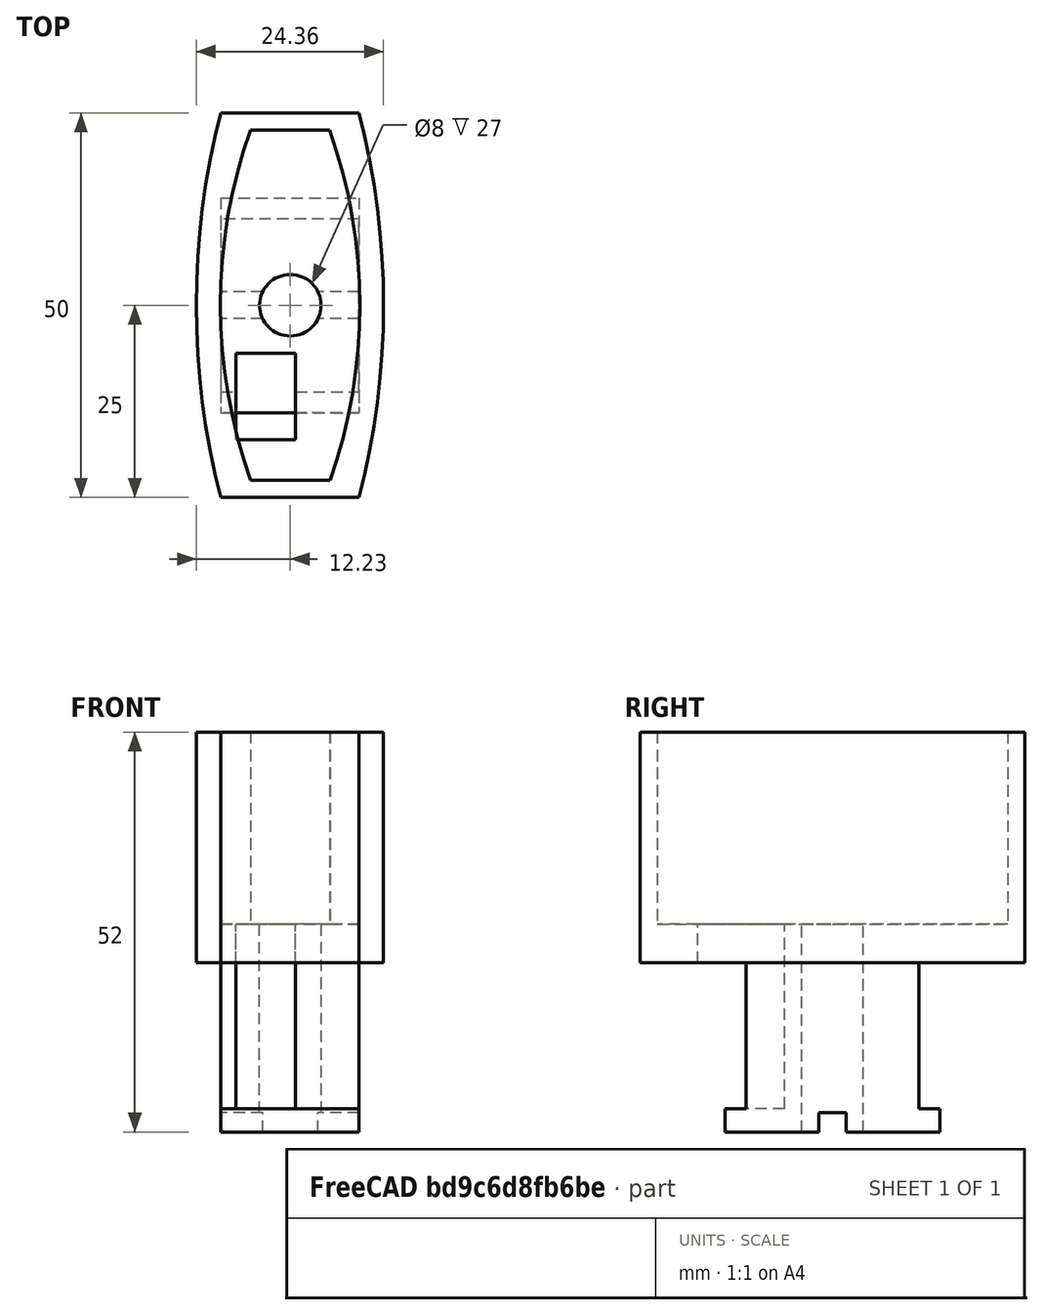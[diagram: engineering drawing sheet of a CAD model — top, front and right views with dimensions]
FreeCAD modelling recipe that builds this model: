
FCSTD DOCUMENT  (FreeCAD 0.18R4 (GitTag))
Label: theta_v_holder
License: All rights reserved
LicenseURL: http://en.wikipedia.org/wiki/All_rights_reserved
objects: Sketcher::SketchObject×7, PartDesign::Pocket×4, PartDesign::Pad×3, PartDesign::Body×1
note: 22 computed .brp shape members not serialized (recipe doc carries the construction recipe); baked Part::Feature solids carry a one-line shape summary decoded from their .brp

FEATURE [Sketcher::SketchObject] Sketch  label="base_sketch"
  MapMode = 5
  Support = -> [XY_Plane]
  sketch-geometry (4):
    g0: LineSegment StartX=0 StartY=0 StartZ=0 EndX=18 EndY=0 EndZ=0
    g1: LineSegment StartX=18 StartY=50 StartZ=0 EndX=0 EndY=50 EndZ=0
    g2: ArcOfCircle CenterX=-78.8246 CenterY=25 CenterZ=0 NormalX=0 NormalY=0 NormalZ=1 AngleXU=0 Radius=100 StartAngle=6.03051 EndAngle=6.53587
    g3: ArcOfCircle CenterX=96.8246 CenterY=25 CenterZ=0 NormalX=0 NormalY=0 NormalZ=1 AngleXU=0 Radius=100 StartAngle=2.88891 EndAngle=3.39427
  constraints (13):
    c: Horizontal(g0)
    c: Horizontal(g1)
    c: Coincident(g0,g-1)
    c: Distance(g1) = 18
    c: Equal(g0,g1)
    c: Coincident(g2,g0)
    c: Coincident(g2,g1)
    c: DistanceY(g0,g1) = 50
    c: Radius(g2) = 100
    c: Coincident(g3,g1)
    c: Coincident(g3,g0)
    c: Equal(g3,g2)
    c: DistanceX(g0,g1) = 0
FEATURE [PartDesign::Pad] Pad
  Length = 30
  Length2 = 100
  Profile = -> Sketch
  Reversed = true
  Type = 0
FEATURE [Sketcher::SketchObject] Sketch001
  MapMode = 5
  Support = -> [XY_Plane]
  sketch-geometry (5):
    g0: LineSegment StartX=3.9 StartY=2.225 StartZ=0 EndX=14.2 EndY=2.225 EndZ=0
    g1: LineSegment StartX=14.15 StartY=47.775 StartZ=0 EndX=3.85 EndY=47.775 EndZ=0
    g2: LineSegment StartX=-0.05 StartY=25 StartZ=0 EndX=18.1 EndY=25 EndZ=0
    g3: ArcOfCircle CenterX=67.9891 CenterY=25.0704 CenterZ=0 NormalX=0 NormalY=0 NormalZ=1 AngleXU=0 Radius=68.0391 StartAngle=2.80137 EndAngle=3.48401
    g4: ArcOfCircle CenterX=-49.9391 CenterY=24.9296 CenterZ=0 NormalX=0 NormalY=0 NormalZ=1 AngleXU=0 Radius=68.0391 StartAngle=5.94296 EndAngle=6.62561
  constraints (18):
    c: Horizontal(g0)
    c: Horizontal(g1)
    c: DistanceY(g-1,g0) = 2.225
    c: DistanceY(g0,g1) = 45.55
    c: Horizontal(g2)
    c: Distance(g2) = 18.15
    c: DistanceY(g0,g2) = 22.775
    c: Coincident(g3,g1)
    c: Coincident(g3,g0)
    c: PointOnObject(g2,g3)
    c: Coincident(g4,g1)
    c: Coincident(g4,g0)
    c: PointOnObject(g2,g4)
    c: Distance(g1) = 10.3
    c: Distance(g0) = 10.3
    c: DistanceX(g-1,g0) = 3.9
    c: DistanceX(g-1,g1) = 3.85
    c: DistanceX(g2,g0) = 3.95
FEATURE [PartDesign::Pocket] Pocket  label="cutout"
  BaseFeature = -> Pad
  Length = 25
  Length2 = 100
  Profile = -> Sketch001
  Type = 0
FEATURE [Sketcher::SketchObject] Sketch002  label="screw_sketch"
  MapMode = 5
  Placement = pos=(0,0,-25) rot=(0,0,1;0rad)
  Support = -> [Pocket]
  sketch-geometry (1):
    g0: Circle CenterX=9.05 CenterY=25 CenterZ=0 NormalX=0 NormalY=0 NormalZ=1 AngleXU=0 Radius=4
  constraints (3):
    c: Diameter(g0) = 8
    c: DistanceY(g-1,g0) = 25
    c: DistanceX(g-1,g0) = 9.05
FEATURE [Sketcher::SketchObject] Sketch004
  MapMode = 5
  Placement = pos=(0,0,-30) rot=(1,0,0;3.14159rad)
  sketch-geometry (4):
    g0: LineSegment StartX=0 StartY=-13.75 StartZ=0 EndX=18 EndY=-13.75 EndZ=0
    g1: LineSegment StartX=18 StartY=-13.75 StartZ=0 EndX=18 EndY=-36.25 EndZ=0
    g2: LineSegment StartX=18 StartY=-36.25 StartZ=0 EndX=0 EndY=-36.25 EndZ=0
    g3: LineSegment StartX=0 StartY=-36.25 StartZ=0 EndX=0 EndY=-13.75 EndZ=0
  constraints (12):
    c: Coincident(g0,g1)
    c: Coincident(g1,g2)
    c: Coincident(g2,g3)
    c: Coincident(g3,g0)
    c: Horizontal(g0)
    c: Horizontal(g2)
    c: Vertical(g1)
    c: Vertical(g3)
    c: PointOnObject(g0,g-2)
    c: Distance(g1) = 22.5
    c: Distance(g0) = 18
    c: DistanceY(g0) = -13.75
FEATURE [PartDesign::Pad] Pad001  label="standoff"
  BaseFeature = -> Pocket
  Length = 19
  Length2 = 100
  Profile = -> Sketch004
  Type = 0
FEATURE [PartDesign::Body] Body
  Group = -> [Sketch,Pad,Sketch001,Pocket,Sketch002,Sketch003,Sketch004,Pad001,Pocket002,Sketch005,Sketch006,Pad002,Pocket003,Pocket001]
  Origin = -> Origin
  Tip = -> Pocket001
FEATURE [PartDesign::Pocket] Pocket001  label="tripod_screw"
  BaseFeature = -> Pocket003
  Length = 35
  Length2 = 5
  Profile = -> Sketch002
  Type = 4
FEATURE [Sketcher::SketchObject] Sketch003
  MapMode = 5
  Placement = pos=(0,0,-30) rot=(1,0,0;3.14159rad)
  Support = -> [Pocket001]
  sketch-geometry (4):
    g0: LineSegment StartX=2 StartY=-7.5 StartZ=0 EndX=9.75 EndY=-7.5 EndZ=0
    g1: LineSegment StartX=9.75 StartY=-7.5 StartZ=0 EndX=9.75 EndY=-18.75 EndZ=0
    g2: LineSegment StartX=9.75 StartY=-18.75 StartZ=0 EndX=2 EndY=-18.75 EndZ=0
    g3: LineSegment StartX=2 StartY=-18.75 StartZ=0 EndX=2 EndY=-7.5 EndZ=0
  constraints (12):
    c: Coincident(g0,g1)
    c: Coincident(g1,g2)
    c: Coincident(g2,g3)
    c: Coincident(g3,g0)
    c: Horizontal(g0)
    c: Horizontal(g2)
    c: Vertical(g1)
    c: Vertical(g3)
    c: Distance(g0) = 7.75
    c: Distance(g3) = 11.25
    c: DistanceX(g-1,g1) = 9.75
    c: DistanceY(g0,g-1) = 7.5
FEATURE [PartDesign::Pocket] Pocket002  label="micro_USB"
  BaseFeature = -> Pad001
  Length = 5
  Length2 = 24
  Profile = -> Sketch003
  Type = 4
FEATURE [Sketcher::SketchObject] Sketch005
  MapMode = 5
  Placement = pos=(0,13.75,0) rot=(1,0,0;1.5708rad)
  Support = -> [Pocket001]
  sketch-geometry (4):
    g0: LineSegment StartX=0 StartY=-48.95 StartZ=0 EndX=18 EndY=-48.95 EndZ=0
    g1: LineSegment StartX=18 StartY=-48.95 StartZ=0 EndX=18 EndY=-52 EndZ=0
    g2: LineSegment StartX=18 StartY=-52 StartZ=0 EndX=0 EndY=-52 EndZ=0
    g3: LineSegment StartX=0 StartY=-52 StartZ=0 EndX=0 EndY=-48.95 EndZ=0
  constraints (11):
    c: Coincident(g0,g1)
    c: Coincident(g1,g2)
    c: Coincident(g2,g3)
    c: Coincident(g3,g0)
    c: Horizontal(g0)
    c: Horizontal(g2)
    c: Vertical(g1)
    c: Vertical(g3)
    c: Distance(g2) = 18
    c: Distance(g1) = 3.05
    c: DistanceY(g2,g-1) = 52
FEATURE [Sketcher::SketchObject] Sketch006
  MapMode = 5
  Placement = pos=(18,0,0) rot=(0.57735,0.57735,0.57735;2.0944rad)
  Support = -> [Pocket001]
  sketch-geometry (4):
    g0: LineSegment StartX=23.25 StartY=-52 StartZ=0 EndX=26.75 EndY=-52 EndZ=0
    g1: LineSegment StartX=26.75 StartY=-52 StartZ=0 EndX=26.75 EndY=-49.5 EndZ=0
    g2: LineSegment StartX=26.75 StartY=-49.5 StartZ=0 EndX=23.25 EndY=-49.5 EndZ=0
    g3: LineSegment StartX=23.25 StartY=-49.5 StartZ=0 EndX=23.25 EndY=-52 EndZ=0
  constraints (12):
    c: Coincident(g0,g1)
    c: Coincident(g1,g2)
    c: Coincident(g2,g3)
    c: Coincident(g3,g0)
    c: Horizontal(g0)
    c: Horizontal(g2)
    c: Vertical(g1)
    c: Vertical(g3)
    c: Distance(g1) = 2.5
    c: Distance(g2) = 3.5
    c: DistanceY(g2,g-1) = 49.5
    c: DistanceX(g-1,g2) = 23.25
FEATURE [PartDesign::Pad] Pad002  label="side_rails"
  BaseFeature = -> Pocket002
  Length = 2.73
  Length2 = 25.23
  Profile = -> Sketch005
  Type = 4
FEATURE [PartDesign::Pocket] Pocket003
  BaseFeature = -> Pad002
  Length = 5
  Length2 = 100
  Profile = -> Sketch006
  Type = 2
